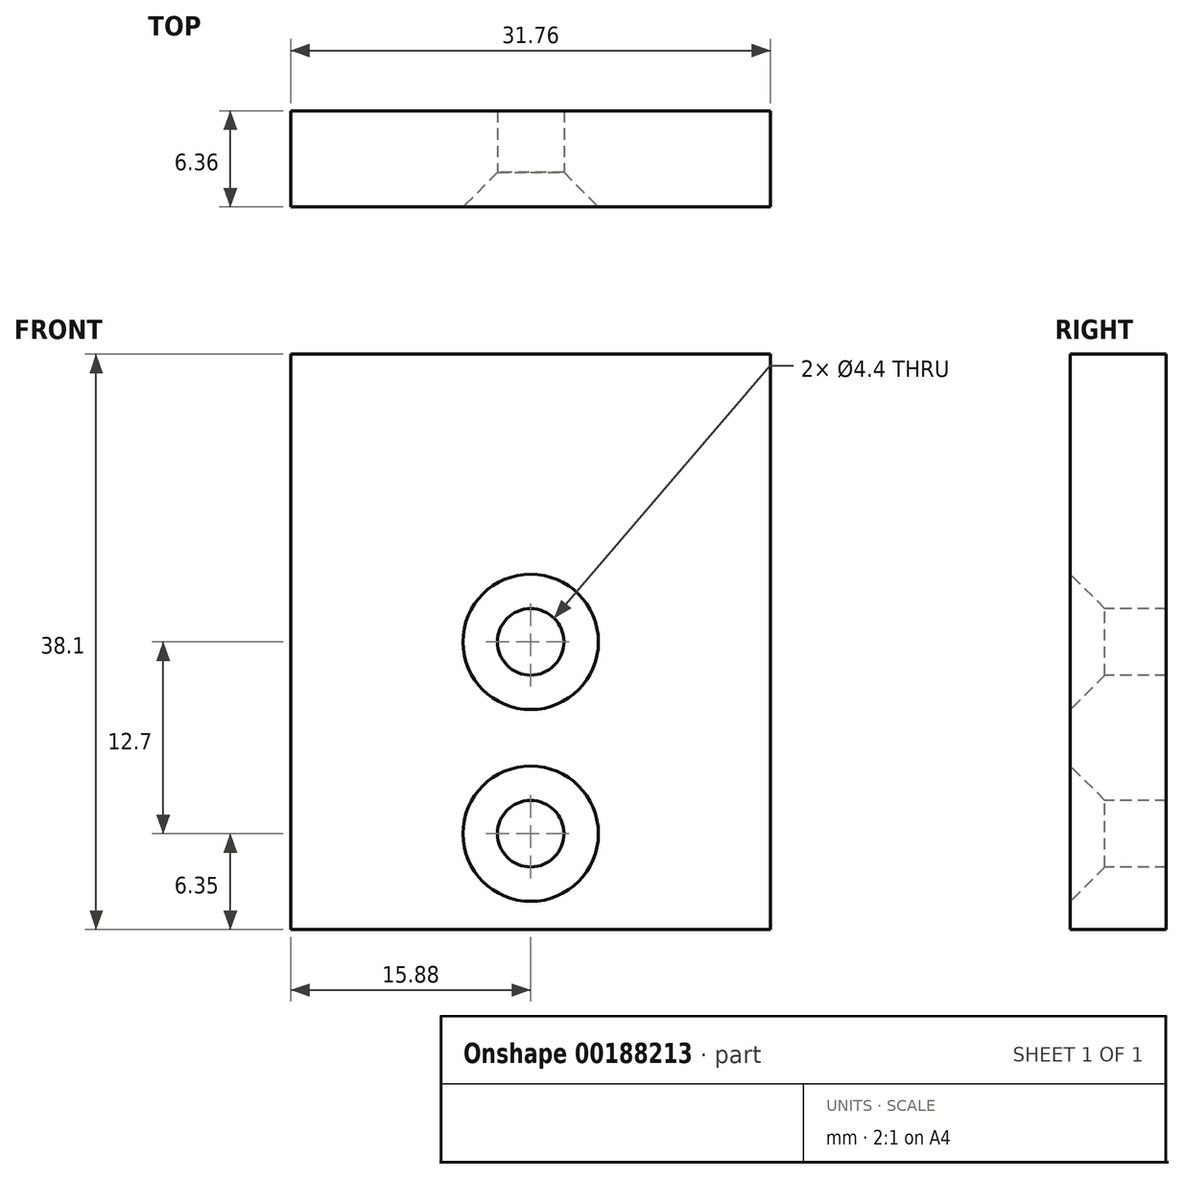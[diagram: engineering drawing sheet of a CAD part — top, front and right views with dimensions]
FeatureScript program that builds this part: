
annotation { "Feature Type Name" : "Feature", "Feature Type Description" : "" }
export const myFeature = defineFeature(function(context is Context, id is Id, definition is map)
    precondition{}
    {
        {
            var Q0;
            Q0=qCreatedBy(makeId("Front.planeOp"),FACE);
            var sketch = newSketch(context, id + "F0", { "sketchPlane" : qUnion([Q0])});
            skLineSegment(sketch, "E0.bottom", {"start": v(-15.87, 19.05) * mm, "end": v(15.88, 19.05) * mm});
            skLineSegment(sketch, "E0.top", {"start": v(-15.88, -19.05) * mm, "end": v(15.87, -19.05) * mm});
            skLineSegment(sketch, "E0.left", {"start": v(-15.87, 19.05) * mm, "end": v(-15.88, -19.05) * mm});
            skLineSegment(sketch, "E0.right", {"start": v(15.88, 19.05) * mm, "end": v(15.87, -19.05) * mm});
            skPoint(sketch, "E0.middle", {"position": v(0, 0) * mm});
            skSolve(sketch);
        }
        {
            var Q0;
            Q0 = qSketchRegion(id + "F0", true);
            extrude(context, id + "F1", {"entities" : qUnion([Q0]), "endBound" : BoundingType.SYMMETRIC, "depth" : 6.35 * mm});
        }
        {
            var Q0;
            Q0=makeQuery(id+"F1.opExtrude","CAP_FACE",FACE,{"disambiguationData":[OSD([sQuery(id+"F0.wireOp",EDGE,"E0.bottom"),sQuery(id+"F0.wireOp",EDGE,"E0.top"),sQuery(id+"F0.wireOp",EDGE,"E0.left"),sQuery(id+"F0.wireOp",EDGE,"E0.right")])],"isStart":false});
            var sketch = newSketch(context, id + "F2", { "sketchPlane" : qUnion([Q0])});
            skPoint(sketch, "E1", {"position": v(0, -12.7) * mm});
            skPoint(sketch, "E2", {"position": v(0, 0) * mm});
            skSolve(sketch);
        }
        {
            var Q0;
            Q0=sQuery(id+"F2.wireOp",VERTEX,"E2");
            var Q1;
            Q1=sQuery(id+"F2.wireOp",VERTEX,"E1");
            var Q2;
            Q2=makeQuery(id+"F1.opExtrude","SWEPT_BODY",BODY,{"disambiguationData":[OSD([sQuery(id+"F0.wireOp",EDGE,"E0.bottom"),sQuery(id+"F0.wireOp",EDGE,"E0.top"),sQuery(id+"F0.wireOp",EDGE,"E0.left"),sQuery(id+"F0.wireOp",EDGE,"E0.right")])]});
            hole(context, id + "F3", {"style" : HoleStyle.C_SINK, "endStyle" : HoleEndStyle.BLIND, "standardTappedOrClearance" : lookupTablePath({ "standard" : "ISO", "fit" : "Normal", "size" : "M4", "type" : "Clearance" }), "standardBlindInLast" : lookupTablePath({ "fit" : "Standard", "standard" : "ISO", "size" : "M4", "type" : "Clearance" }), "holeDiameter" : 4.4 * mm, "cSinkDiameter" : 8.96 * mm, "cSinkAngle" : 90 * degree, "holeDepth" : 12.7 * mm, "startFromSketch" : true, "locations" : qUnion([Q0, Q1]), "scope" : qUnion([Q2])});
        }
    });
